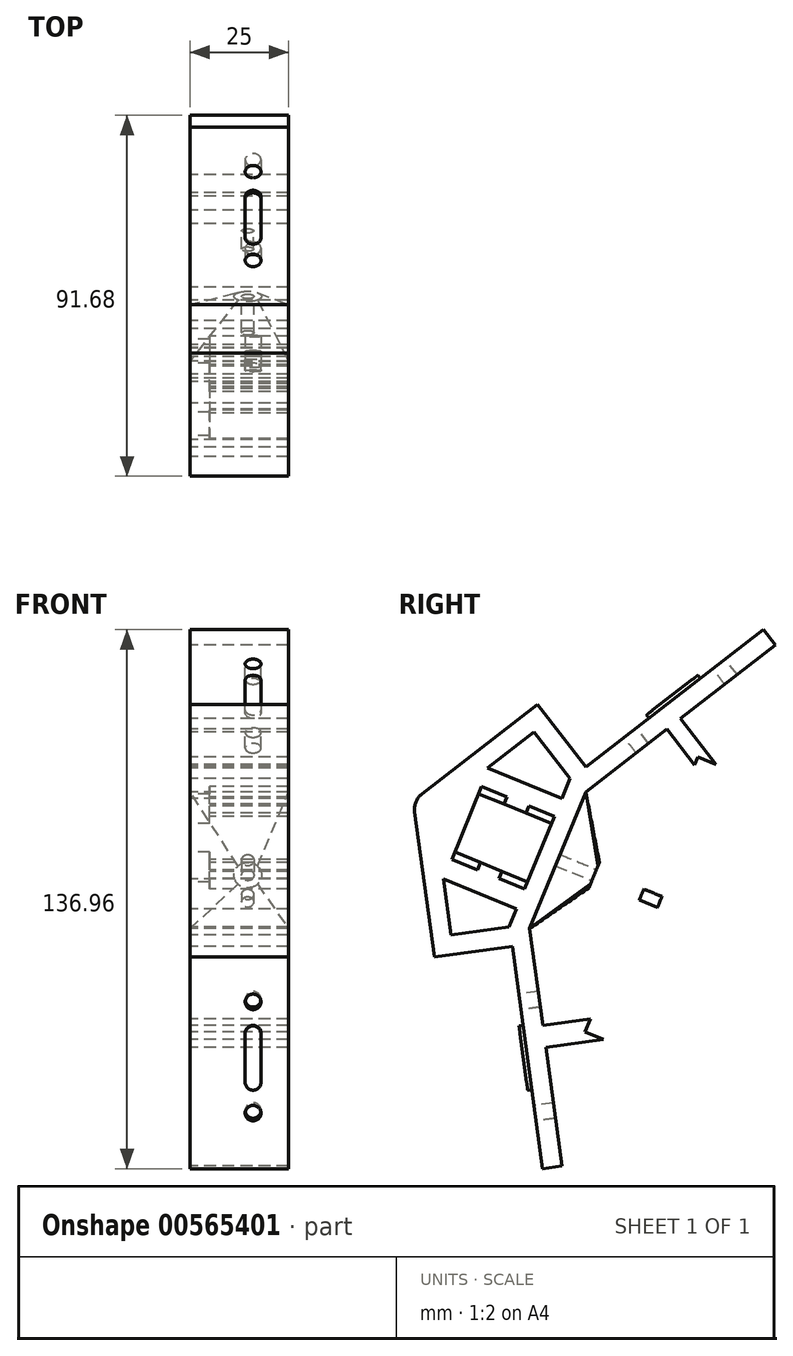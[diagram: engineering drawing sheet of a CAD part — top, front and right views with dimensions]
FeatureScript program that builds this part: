
annotation { "Feature Type Name" : "Feature", "Feature Type Description" : "" }
export const myFeature = defineFeature(function(context is Context, id is Id, definition is map)
    precondition{}
    {
        {
            var Q0;
            Q0=qCreatedBy(makeId("Right.planeOp"),FACE);
            var sketch = newSketch(context, id + "F0", { "sketchPlane" : qUnion([Q0])});
            skLineSegment(sketch, "E0", {"start": v(-33.6, 14.18) * mm, "end": v(-1.95, 38.65) * mm});
            skLineSegment(sketch, "E1", {"start": v(-1.95, 38.65) * mm, "end": v(10.28, 22.83) * mm});
            skLineSegment(sketch, "E2", {"start": v(-8.4, -22.77) * mm, "end": v(-28.23, -25.46) * mm});
            skLineSegment(sketch, "E3", {"start": v(-28.23, -25.46) * mm, "end": v(-33.6, 14.18) * mm});
            skLineSegment(sketch, "E4", {"start": v(10.28, 22.83) * mm, "end": v(55.37, 57.7) * mm});
            skLineSegment(sketch, "E5", {"start": v(55.37, 57.7) * mm, "end": v(58.43, 53.74) * mm});
            skLineSegment(sketch, "E6", {"start": v(58.43, 53.74) * mm, "end": v(10.28, 16.5) * mm});
            skLineSegment(sketch, "E7", {"start": v(10.28, 16.5) * mm, "end": v(-3.97, -18.27) * mm});
            skLineSegment(sketch, "E8", {"start": v(-3.97, -18.27) * mm, "end": v(4.2, -78.59) * mm});
            skLineSegment(sketch, "E9", {"start": v(4.2, -78.59) * mm, "end": v(-0.75, -79.26) * mm});
            skLineSegment(sketch, "E10", {"start": v(-0.75, -79.26) * mm, "end": v(-8.4, -22.77) * mm});
            skPoint(sketch, "E11", {"position": v(34.35, 35.12) * mm});
            skPoint(sketch, "E12", {"position": v(0.11, -48.43) * mm});
            skLineSegment(sketch, "E13", {"start": v(34.35, 35.12) * mm, "end": v(43.38, 23.45) * mm});
            skLineSegment(sketch, "E14", {"start": v(43.38, 23.45) * mm, "end": v(14.74, -46.45) * mm});
            skLineSegment(sketch, "E15", {"start": v(14.74, -46.45) * mm, "end": v(0.11, -48.43) * mm});
            skLineSegment(sketch, "E16", {"start": v(11.49, -41.2) * mm, "end": v(37.94, 23.35) * mm});
            skLineSegment(sketch, "E17", {"start": v(2.32, 10.27) * mm, "end": v(-16.19, 17.85) * mm});
            skLineSegment(sketch, "E18", {"start": v(-16.19, 17.85) * mm, "end": v(-23.77, -0.65) * mm});
            skLineSegment(sketch, "E19", {"start": v(-23.77, -0.65) * mm, "end": v(-5.26, -8.24) * mm});
            skLineSegment(sketch, "E20", {"start": v(-5.26, -8.24) * mm, "end": v(2.32, 10.27) * mm});
            skLineSegment(sketch, "E21", {"start": v(37.94, 23.35) * mm, "end": v(30.9, 32.45) * mm});
            skLineSegment(sketch, "E22", {"start": v(11.49, -41.2) * mm, "end": v(-0.64, -42.85) * mm});
            skPoint(sketch, "E23", {"position": v(3.15, -0.88) * mm});
            skPoint(sketch, "E24", {"position": v(-1.47, 1.01) * mm});
            skLineSegment(sketch, "E25", {"start": v(3.15, -0.88) * mm, "end": v(-1.47, 1.01) * mm});
            skLineSegment(sketch, "E26", {"start": v(1.56, 8.42) * mm, "end": v(-16.94, 16) * mm});
            skLineSegment(sketch, "E27", {"start": v(-4.5, -6.39) * mm, "end": v(-23.01, 1.2) * mm});
            skLineSegment(sketch, "E28", {"start": v(-11.74, -5.58) * mm, "end": v(-10.98, -3.73) * mm});
            skLineSegment(sketch, "E29", {"start": v(-17.3, -3.3) * mm, "end": v(-16.53, -1.46) * mm});
            skLineSegment(sketch, "E30", {"start": v(-10.47, 13.35) * mm, "end": v(-9.7, 15.2) * mm});
            skPoint(sketch, "E31", {"position": v(-14.52, -4.45) * mm});
            skPoint(sketch, "E32", {"position": v(-6.93, 14.06) * mm});
            skLineSegment(sketch, "E33", {"start": v(-4.92, 11.07) * mm, "end": v(-4.16, 12.92) * mm});
            skLineSegment(sketch, "E34", {"start": v(-2.85, 31.63) * mm, "end": v(6.25, 19.86) * mm});
            skLineSegment(sketch, "E35", {"start": v(6.25, 19.86) * mm, "end": v(4.17, 14.8) * mm});
            skLineSegment(sketch, "E36", {"start": v(4.17, 14.8) * mm, "end": v(-14.65, 22.5) * mm});
            skLineSegment(sketch, "E37", {"start": v(-14.65, 22.5) * mm, "end": v(-2.85, 31.63) * mm});
            skLineSegment(sketch, "E38", {"start": v(-7.31, -13.24) * mm, "end": v(-9.2, -17.83) * mm});
            skLineSegment(sketch, "E39", {"start": v(-9.2, -17.83) * mm, "end": v(-23.94, -19.83) * mm});
            skLineSegment(sketch, "E40", {"start": v(-23.94, -19.83) * mm, "end": v(-25.87, -5.64) * mm});
            skPoint(sketch, "E40.endSnap0", {"position": v(-30.91, -5.64) * mm});
            skLineSegment(sketch, "E41", {"start": v(-25.87, -5.64) * mm, "end": v(-7.31, -13.24) * mm});
            skSolve(sketch);
        }
        {
            var Q0;
            Q0=makeQuery(id+"F0.imprint","IMPRINT",FACE,{"disambiguationData":[TD([[makeQuery(id+"F0.imprint","IMPRINT",EDGE,{"derivedFrom":sQuery(id+"F0.wireOp",EDGE,"E0")}),-1.0]])]});
            var Q1;
            {var subQ0=sQuery(id+"F0.wireOp",EDGE,"E30");Q1=makeQuery(id+"F0.imprint","IMPRINT",FACE,{"disambiguationData":[TD([[makeQuery(id+"F0.imprint","IMPRINT",EDGE,{"derivedFrom":subQ0}),-1.0]])]});}
            var Q2;
            {var subQ0=sQuery(id+"F0.wireOp",EDGE,"E28");Q2=makeQuery(id+"F0.imprint","IMPRINT",FACE,{"disambiguationData":[TD([[makeQuery(id+"F0.imprint","IMPRINT",EDGE,{"derivedFrom":subQ0}),1.0]])]});}
            var Q3;
            {var subQ0=sQuery(id+"F0.wireOp",EDGE,"E13");Q3=makeQuery(id+"F0.imprint","IMPRINT",FACE,{"disambiguationData":[TD([[makeQuery(id+"F0.imprint","IMPRINT",EDGE,{"derivedFrom":subQ0}),-1.0]])]});}
            extrude(context, id + "F1", {"entities" : qUnion([Q0, Q1, Q2, Q3]), "depth" : 25 * mm, "offsetDistance" : 25 * mm});
        }
        {
            var Q0;
            {var subQ3=sQuery(id+"F0.wireOp",EDGE,"E30");Q0=makeQuery(id+"F0.imprint","IMPRINT",FACE,{"disambiguationData":[TD([[makeQuery(id+"F0.imprint","IMPRINT",EDGE,{"derivedFrom":subQ3}),1.0]])]});}
            var Q1;
            {var subQ3=sQuery(id+"F0.wireOp",EDGE,"E33");Q1=makeQuery(id+"F0.imprint","IMPRINT",FACE,{"disambiguationData":[TD([[makeQuery(id+"F0.imprint","IMPRINT",EDGE,{"derivedFrom":subQ3}),-1.0]])]});}
            var Q2;
            {var subQ5=sQuery(id+"F0.wireOp",EDGE,"E29");Q2=makeQuery(id+"F0.imprint","IMPRINT",FACE,{"disambiguationData":[TD([[makeQuery(id+"F0.imprint","IMPRINT",EDGE,{"derivedFrom":subQ5}),1.0]])]});}
            var Q3;
            {var subQ3=sQuery(id+"F0.wireOp",EDGE,"E28");Q3=makeQuery(id+"F0.imprint","IMPRINT",FACE,{"disambiguationData":[TD([[makeQuery(id+"F0.imprint","IMPRINT",EDGE,{"derivedFrom":subQ3}),-1.0]])]});}
            extrude(context, id + "F2", {"entities" : qUnion([Q0, Q1, Q2, Q3]), "operationType" : NewBodyOperationType.ADD, "depth" : 5 * mm, "offsetDistance" : 25 * mm});
        }
        {
            var Q0;
            Q0=makeQuery(id+"F1.opExtrude","SWEPT_EDGE",EDGE,{"disambiguationData":[OSD([sQuery(id+"F0.wireOp",EDGE,"E0"),sQuery(id+"F0.wireOp",EDGE,"E3")])]});
            fillet(context, id + "F3", {"entities" : qUnion([Q0]), "radius" : 5 * mm, "tangentPropagation" : true, "allowEdgeOverflow" : false});
        }
        {
            var Q0;
            Q0=makeQuery(id+"F1.opExtrude","SWEPT_FACE",FACE,{"disambiguationData":[OSD([sQuery(id+"F0.wireOp",EDGE,"E14")])]});
            var sketch = newSketch(context, id + "F4", { "sketchPlane" : qUnion([Q0])});
            skLineSegment(sketch, "E42", {"start": v(-25, -32.56) * mm, "end": v(-18.2, 0.38) * mm});
            skLineSegment(sketch, "E43", {"start": v(-18.2, 0.38) * mm, "end": v(-25, 33.32) * mm});
            skLineSegment(sketch, "E44", {"start": v(-11.04, 0.38) * mm, "end": v(0, 32.15) * mm});
            skLineSegment(sketch, "E45", {"start": v(-11.04, 0.38) * mm, "end": v(0, -31.39) * mm});
            skLineSegment(sketch, "E46", {"start": v(-18.2, 0.38) * mm, "end": v(-11.04, 0.38) * mm});
            skCircle(sketch, "E47", {"center": v(-14.62, 0.38) * mm, "radius": 1.5 * mm});
            skLineSegment(sketch, "E48", {"start": v(-20, -32.39) * mm, "end": v(-4.83, -32.39) * mm});
            skLineSegment(sketch, "E49", {"start": v(-20, 33.15) * mm, "end": v(-5, 33.15) * mm});
            skLineSegment(sketch, "E50", {"start": v(-5, 33.15) * mm, "end": v(-14.33, 6.3) * mm});
            skLineSegment(sketch, "E51", {"start": v(-20, 33.15) * mm, "end": v(-14.33, 6.3) * mm});
            skLineSegment(sketch, "E52", {"start": v(-4.83, -32.39) * mm, "end": v(-14.26, -5.23) * mm});
            skLineSegment(sketch, "E53", {"start": v(-14.26, -5.23) * mm, "end": v(-20, -32.39) * mm});
            skSolve(sketch);
        }
        {
            var Q0;
            {var subQ0=sQuery(id+"F4.wireOp",EDGE,"E42");Q0=makeQuery(id+"F4.imprint","IMPRINT",FACE,{"disambiguationData":[TD([[makeQuery(id+"F4.imprint","IMPRINT",EDGE,{"derivedFrom":subQ0}),1.0]])]});}
            var Q1;
            Q1=makeQuery(id+"F4.imprint","IMPRINT",FACE,{"disambiguationData":[TD([[makeQuery(id+"F4.imprint","IMPRINT",EDGE,{"derivedFrom":sQuery(id+"F4.wireOp",EDGE,"E48")}),1.0]])]});
            var Q2;
            Q2=makeQuery(id+"F4.imprint","IMPRINT",FACE,{"disambiguationData":[TD([[makeQuery(id+"F4.imprint","IMPRINT",EDGE,{"derivedFrom":sQuery(id+"F4.wireOp",EDGE,"fZY6cRj9-U6Pt-Djpp-X8S6-NcBkGdGhvJ9b")}),1.0]])]});
            var Q3;
            {var subQ0=sQuery(id+"F4.wireOp",EDGE,"E44");Q3=makeQuery(id+"F4.imprint","IMPRINT",FACE,{"disambiguationData":[TD([[makeQuery(id+"F4.imprint","IMPRINT",EDGE,{"derivedFrom":subQ0}),-1.0]])]});}
            var Q4;
            {var subQ0=sQuery(id+"F4.wireOp",EDGE,"E47");var subQ1=sQuery(id+"F4.wireOp",EDGE,"E46");var subQ2=makeQuery(id+"F4.imprint","INTERSECT",VERTEX,{"disambiguationData":[OD(0.0)],"derivedFrom":[subQ1,subQ0]});Q4=makeQuery(id+"F4.imprint","IMPRINT",FACE,{"disambiguationData":[TD([[makeQuery(id+"F4.imprint","IMPRINT",EDGE,{"disambiguationData":[TD([[subQ2,-1.0]])],"derivedFrom":subQ1}),1.0]])]});}
            var Q5;
            {var subQ0=sQuery(id+"F4.wireOp",EDGE,"E47");var subQ1=sQuery(id+"F4.wireOp",EDGE,"E46");var subQ2=makeQuery(id+"F4.imprint","INTERSECT",VERTEX,{"disambiguationData":[OD(0.0)],"derivedFrom":[subQ1,subQ0]});Q5=makeQuery(id+"F4.imprint","IMPRINT",FACE,{"disambiguationData":[TD([[makeQuery(id+"F4.imprint","IMPRINT",EDGE,{"disambiguationData":[TD([[subQ2,-1.0]])],"derivedFrom":subQ1}),-1.0]])]});}
            var Q6;
            {var subQ0=sQuery(id+"F4.wireOp",EDGE,"E49");Q6=makeQuery(id+"F4.imprint","IMPRINT",FACE,{"disambiguationData":[TD([[makeQuery(id+"F4.imprint","IMPRINT",EDGE,{"derivedFrom":subQ0}),-1.0]])]});}
            extrude(context, id + "F5", {"entities" : qUnion([Q0, Q1, Q2, Q3, Q4, Q5, Q6]), "operationType" : NewBodyOperationType.REMOVE, "oppositeDirection" : true, "depth" : 5 * mm, "offsetDistance" : 25 * mm});
        }
        {
            var Q0;
            Q0=makeQuery(id+"F1.opExtrude","SWEPT_FACE",FACE,{"disambiguationData":[OSD([sQuery(id+"F0.wireOp",EDGE,"E7")])]});
            var sketch = newSketch(context, id + "F6", { "sketchPlane" : qUnion([Q0])});
            skLineSegment(sketch, "E54", {"start": v(-25, -18.41) * mm, "end": v(-25, 19.17) * mm});
            skLineSegment(sketch, "E55", {"start": v(-25, 19.17) * mm, "end": v(0, 19.17) * mm});
            skLineSegment(sketch, "E56", {"start": v(0, 19.17) * mm, "end": v(0, -18.41) * mm});
            skLineSegment(sketch, "E57", {"start": v(0, -18.41) * mm, "end": v(-25, -18.41) * mm});
            skSolve(sketch);
        }
        {
            var Q0;
            Q0=makeQuery(id+"F6.imprint","IMPRINT",FACE,{"disambiguationData":[TD([[makeQuery(id+"F6.imprint","IMPRINT",EDGE,{"derivedFrom":sQuery(id+"F6.wireOp",EDGE,"E54")}),1.0]])]});
            cPlane(context, id + "F7", {"entities" : qUnion([Q0]), "cplaneType" : CPlaneType.OFFSET, "offset" : 10 * mm, "width" : 150 * mm, "height" : 150 * mm});
        }
        {
            var Q0;
            Q0=qCreatedBy(id+"F7.planeOp",FACE);
            var sketch = newSketch(context, id + "F8", { "sketchPlane" : qUnion([Q0])});
            skPoint(sketch, "E58.first.point", {"position": v(-16.2, 0.23) * mm});
            skPoint(sketch, "E58.second.point", {"position": v(-14.11, 1.83) * mm});
            skPoint(sketch, "E58.third.point", {"position": v(-13.8, -0.91) * mm});
            skPoint(sketch, "E59.first.point", {"position": v(-18.15, 0.42) * mm});
            skPoint(sketch, "E59.second.point", {"position": v(-13.3, 3.61) * mm});
            skPoint(sketch, "E59.third.point", {"position": v(-12.35, -2.25) * mm});
            skArc(sketch, "E60", {"start": v(-17.12, -2.1) * mm, "mid": v(-14.65, -3.12) * mm, "end": v(-12.18, -2.1) * mm});
            skArc(sketch, "E61", {"start": v(-17.12, 2.86) * mm, "mid": v(-18.15, 0.38) * mm, "end": v(-17.12, -2.1) * mm});
            skArc(sketch, "E62", {"start": v(-12.18, 2.86) * mm, "mid": v(-14.65, 3.88) * mm, "end": v(-17.12, 2.86) * mm});
            skArc(sketch, "E63", {"start": v(-12.18, -2.1) * mm, "mid": v(-11.15, 0.38) * mm, "end": v(-12.18, 2.86) * mm});
            skSolve(sketch);
        }
        {
            var Q1;
            Q1 = qSketchRegion(id + "F8", true);
            var Q2;
            Q2 = qSketchRegion(id + "F6", true);
            loft(context, id + "F9", {"operationType" : NewBodyOperationType.ADD, "sheetProfilesArray" : [{ "sheetProfileEntities" : qUnion([Q1]) }, { "sheetProfileEntities" : qUnion([Q2]) }]});
        }
        {
            var Q0;
            Q0=makeQuery(id+"F9.opLoft","CAP_FACE",FACE,{"disambiguationData":[OSD([makeQuery(id+"F8.imprint","IMPRINT",FACE,{"disambiguationData":[TD([[makeQuery(id+"F8.imprint","IMPRINT",EDGE,{"derivedFrom":sQuery(id+"F8.wireOp",EDGE,"E60")}),1.0]])]})])],"isStart":true});
            var sketch = newSketch(context, id + "F10", { "sketchPlane" : qUnion([Q0])});
            skCircle(sketch, "E64", {"center": v(-14.65, 0.38) * mm, "radius": 1.55 * mm});
            skSolve(sketch);
        }
        {
            var Q0;
            Q0=makeQuery(id+"F10.imprint","IMPRINT",FACE,{"disambiguationData":[TD([[makeQuery(id+"F10.imprint","IMPRINT",EDGE,{"derivedFrom":sQuery(id+"F10.wireOp",EDGE,"E64")}),1.0]])]});
            extrude(context, id + "F11", {"entities" : qUnion([Q0]), "operationType" : NewBodyOperationType.REMOVE, "oppositeDirection" : true, "depth" : 10 * mm, "offsetDistance" : 25 * mm});
        }
        {
            var Q0;
            Q0=makeQuery(id+"F1.opExtrude","SWEPT_FACE",FACE,{"disambiguationData":[OSD([sQuery(id+"F0.wireOp",EDGE,"E4")])]});
            var sketch = newSketch(context, id + "F12", { "sketchPlane" : qUnion([Q0])});
            skCircle(sketch, "E65", {"center": v(16, 56.85) * mm, "radius": 2 * mm});
            skCircle(sketch, "E66", {"center": v(16, 44.35) * mm, "radius": 2 * mm});
            skLineSegment(sketch, "E67", {"start": v(18, 56.85) * mm, "end": v(18, 44.35) * mm});
            skLineSegment(sketch, "E68", {"start": v(14, 44.35) * mm, "end": v(14, 56.85) * mm});
            skCircle(sketch, "E69", {"center": v(16, 64.85) * mm, "radius": 2 * mm});
            skCircle(sketch, "E70", {"center": v(16, 36.35) * mm, "radius": 2 * mm});
            skLineSegment(sketch, "E71", {"start": v(18, 56.85) * mm, "end": v(18, 64.85) * mm});
            skLineSegment(sketch, "E72", {"start": v(14, 64.85) * mm, "end": v(14, 56.85) * mm});
            skLineSegment(sketch, "E73", {"start": v(18, 44.35) * mm, "end": v(18, 36.35) * mm});
            skLineSegment(sketch, "E74", {"start": v(14, 44.35) * mm, "end": v(14, 36.35) * mm});
            skSolve(sketch);
        }
        {
            var Q0;
            Q0=makeQuery(id+"F1.opExtrude","SWEPT_FACE",FACE,{"disambiguationData":[OSD([sQuery(id+"F0.wireOp",EDGE,"E10")])]});
            var sketch = newSketch(context, id + "F13", { "sketchPlane" : qUnion([Q0])});
            skCircle(sketch, "E75", {"center": v(16, -43.69) * mm, "radius": 2 * mm});
            skCircle(sketch, "E76", {"center": v(16, -56.19) * mm, "radius": 2 * mm});
            skLineSegment(sketch, "E77", {"start": v(18, -43.69) * mm, "end": v(18, -56.19) * mm});
            skLineSegment(sketch, "E78", {"start": v(14, -56.19) * mm, "end": v(14, -43.69) * mm});
            skCircle(sketch, "E79", {"center": v(16, -35.69) * mm, "radius": 2 * mm});
            skCircle(sketch, "E80", {"center": v(16, -64.19) * mm, "radius": 2 * mm});
            skLineSegment(sketch, "E81", {"start": v(18, -43.69) * mm, "end": v(18, -35.69) * mm});
            skLineSegment(sketch, "E82", {"start": v(14, -35.69) * mm, "end": v(14, -43.69) * mm});
            skLineSegment(sketch, "E83", {"start": v(18, -56.19) * mm, "end": v(18, -64.19) * mm});
            skLineSegment(sketch, "E84", {"start": v(14, -56.19) * mm, "end": v(14, -64.19) * mm});
            skSolve(sketch);
        }
        {
            var Q0;
            {var subQ0=sQuery(id+"F13.wireOp",EDGE,"E75");var subQ1=makeQuery(id+"F13.imprint","INTERSECT",VERTEX,{"derivedFrom":[subQ0,sQuery(id+"F13.wireOp",EDGE,"E77")]});Q0=makeQuery(id+"F13.imprint","IMPRINT",FACE,{"disambiguationData":[TD([[makeQuery(id+"F13.imprint","IMPRINT",EDGE,{"disambiguationData":[TD([[subQ1,-1.0]])],"derivedFrom":subQ0}),1.0]])]});}
            var Q1;
            {var subQ0=sQuery(id+"F13.wireOp",EDGE,"E77");Q1=makeQuery(id+"F13.imprint","IMPRINT",FACE,{"disambiguationData":[TD([[makeQuery(id+"F13.imprint","IMPRINT",EDGE,{"derivedFrom":subQ0}),-1.0]])]});}
            var Q2;
            {var subQ0=sQuery(id+"F13.wireOp",EDGE,"E76");var subQ1=makeQuery(id+"F13.imprint","INTERSECT",VERTEX,{"derivedFrom":[subQ0,sQuery(id+"F13.wireOp",EDGE,"E77")]});Q2=makeQuery(id+"F13.imprint","IMPRINT",FACE,{"disambiguationData":[TD([[makeQuery(id+"F13.imprint","IMPRINT",EDGE,{"disambiguationData":[TD([[subQ1,1.0]])],"derivedFrom":subQ0}),1.0]])]});}
            extrude(context, id + "F14", {"entities" : qUnion([Q0, Q1, Q2]), "operationType" : NewBodyOperationType.ADD, "depth" : 1 * mm, "offsetDistance" : 25 * mm});
        }
        {
            var Q0;
            {var subQ0=sQuery(id+"F12.wireOp",EDGE,"E65");var subQ1=makeQuery(id+"F12.imprint","INTERSECT",VERTEX,{"derivedFrom":[subQ0,sQuery(id+"F12.wireOp",EDGE,"E67")]});Q0=makeQuery(id+"F12.imprint","IMPRINT",FACE,{"disambiguationData":[TD([[makeQuery(id+"F12.imprint","IMPRINT",EDGE,{"disambiguationData":[TD([[subQ1,-1.0]])],"derivedFrom":subQ0}),1.0]])]});}
            var Q1;
            {var subQ0=sQuery(id+"F12.wireOp",EDGE,"E67");Q1=makeQuery(id+"F12.imprint","IMPRINT",FACE,{"disambiguationData":[TD([[makeQuery(id+"F12.imprint","IMPRINT",EDGE,{"derivedFrom":subQ0}),-1.0]])]});}
            var Q2;
            {var subQ0=sQuery(id+"F12.wireOp",EDGE,"E66");var subQ1=makeQuery(id+"F12.imprint","INTERSECT",VERTEX,{"derivedFrom":[subQ0,sQuery(id+"F12.wireOp",EDGE,"E67")]});Q2=makeQuery(id+"F12.imprint","IMPRINT",FACE,{"disambiguationData":[TD([[makeQuery(id+"F12.imprint","IMPRINT",EDGE,{"disambiguationData":[TD([[subQ1,1.0]])],"derivedFrom":subQ0}),1.0]])]});}
            extrude(context, id + "F15", {"entities" : qUnion([Q0, Q1, Q2]), "operationType" : NewBodyOperationType.ADD, "depth" : 1 * mm, "offsetDistance" : 25 * mm});
        }
        {
            var Q0;
            {var subQ0=sQuery(id+"F12.wireOp",EDGE,"E69");var subQ1=makeQuery(id+"F12.imprint","INTERSECT",VERTEX,{"derivedFrom":[subQ0,sQuery(id+"F12.wireOp",EDGE,"E71")]});Q0=makeQuery(id+"F12.imprint","IMPRINT",FACE,{"disambiguationData":[TD([[makeQuery(id+"F12.imprint","IMPRINT",EDGE,{"disambiguationData":[TD([[subQ1,-1.0]])],"derivedFrom":subQ0}),1.0]])]});}
            var Q1;
            {var subQ0=sQuery(id+"F12.wireOp",EDGE,"E70");var subQ1=makeQuery(id+"F12.imprint","INTERSECT",VERTEX,{"derivedFrom":[subQ0,sQuery(id+"F12.wireOp",EDGE,"E73")]});Q1=makeQuery(id+"F12.imprint","IMPRINT",FACE,{"disambiguationData":[TD([[makeQuery(id+"F12.imprint","IMPRINT",EDGE,{"disambiguationData":[TD([[subQ1,-1.0]])],"derivedFrom":subQ0}),1.0]])]});}
            extrude(context, id + "F16", {"entities" : qUnion([Q0, Q1]), "operationType" : NewBodyOperationType.REMOVE, "oppositeDirection" : true, "depth" : 5 * mm, "offsetDistance" : 25 * mm});
        }
        {
            var Q0;
            {var subQ0=sQuery(id+"F13.wireOp",EDGE,"E79");var subQ1=makeQuery(id+"F13.imprint","INTERSECT",VERTEX,{"derivedFrom":[subQ0,sQuery(id+"F13.wireOp",EDGE,"E81")]});Q0=makeQuery(id+"F13.imprint","IMPRINT",FACE,{"disambiguationData":[TD([[makeQuery(id+"F13.imprint","IMPRINT",EDGE,{"disambiguationData":[TD([[subQ1,-1.0]])],"derivedFrom":subQ0}),1.0]])]});}
            var Q1;
            {var subQ0=sQuery(id+"F13.wireOp",EDGE,"E80");var subQ1=makeQuery(id+"F13.imprint","INTERSECT",VERTEX,{"derivedFrom":[subQ0,sQuery(id+"F13.wireOp",EDGE,"E83")]});Q1=makeQuery(id+"F13.imprint","IMPRINT",FACE,{"disambiguationData":[TD([[makeQuery(id+"F13.imprint","IMPRINT",EDGE,{"disambiguationData":[TD([[subQ1,-1.0]])],"derivedFrom":subQ0}),1.0]])]});}
            extrude(context, id + "F17", {"entities" : qUnion([Q0, Q1]), "operationType" : NewBodyOperationType.REMOVE, "oppositeDirection" : true, "depth" : 5 * mm, "offsetDistance" : 25 * mm});
        }
    });
